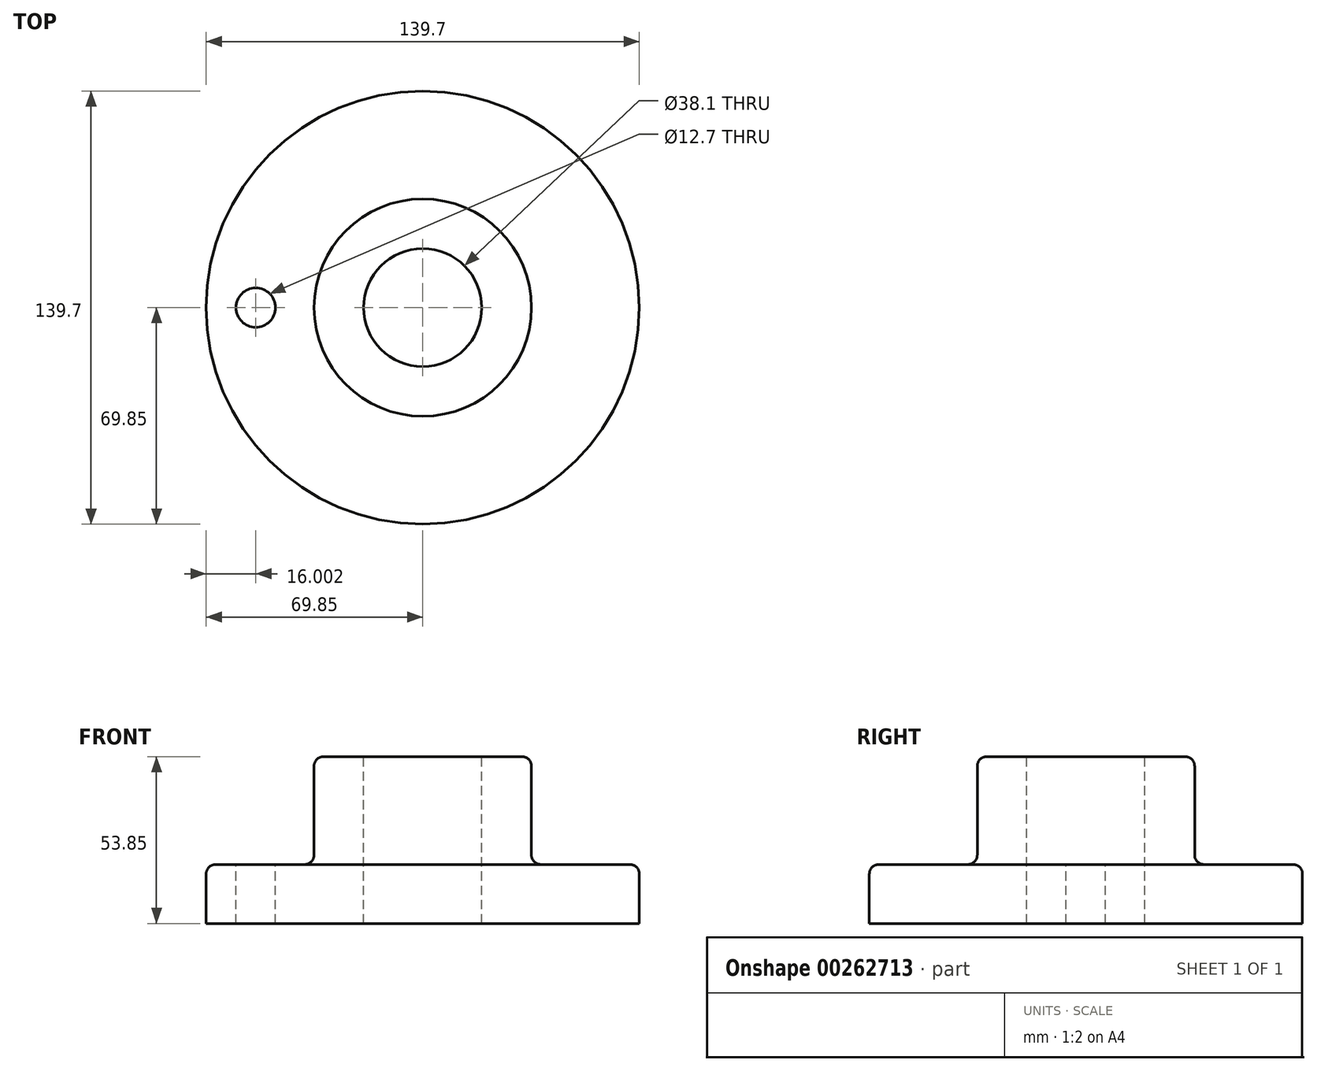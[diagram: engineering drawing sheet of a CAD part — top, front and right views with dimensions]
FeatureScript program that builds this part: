
annotation { "Feature Type Name" : "Feature", "Feature Type Description" : "" }
export const myFeature = defineFeature(function(context is Context, id is Id, definition is map)
    precondition{}
    {
        {
            var Q0;
            Q0=qCreatedBy(makeId("Front.planeOp"),FACE);
            var sketch = newSketch(context, id + "F0", { "sketchPlane" : qUnion([Q0])});
            skLineSegment(sketch, "E0", {"start": v(19.05, 34.8) * mm, "end": v(19.05, -19.05) * mm});
            skLineSegment(sketch, "E1", {"start": v(19.05, -19.05) * mm, "end": v(69.85, -19.05) * mm});
            skLineSegment(sketch, "E2", {"start": v(69.85, -19.05) * mm, "end": v(69.85, 0) * mm});
            skLineSegment(sketch, "E3", {"start": v(69.85, 0) * mm, "end": v(35.05, 0) * mm});
            skLineSegment(sketch, "E4", {"start": v(35.05, 0) * mm, "end": v(35.05, 34.8) * mm});
            skLineSegment(sketch, "E5", {"start": v(35.05, 34.8) * mm, "end": v(19.05, 34.8) * mm});
            skLineSegment(sketch, "E6", {"start": v(0, 35.4) * mm, "end": v(0, -19.17) * mm});
            skSolve(sketch);
        }
        {
            var Q0;
            Q0=makeQuery(id+"F0.imprint","IMPRINT",FACE,{"disambiguationData":[TD([[makeQuery(id+"F0.imprint","IMPRINT",EDGE,{"derivedFrom":sQuery(id+"F0.wireOp",EDGE,"E0")}),1.0]])]});
            var Q1;
            Q1=sQuery(id+"F0.wireOp",EDGE,"E6");
            revolve(context, id + "F1", {"entities" : qUnion([Q0]), "axis" : qUnion([Q1]), "revolveType" : RevolveType.FULL});
        }
        {
            var Q0;
            Q0=makeQuery(id+"F1.opRevolve","SWEPT_FACE",FACE,{"disambiguationData":[OSD([sQuery(id+"F0.wireOp",EDGE,"E3")])]});
            var sketch = newSketch(context, id + "F2", { "sketchPlane" : qUnion([Q0])});
            skCircle(sketch, "E7", {"center": v(0, 0) * mm, "radius": 53.85 * mm});
            skCircle(sketch, "E8", {"center": v(-53.85, 0) * mm, "radius": 6.35 * mm});
            skSolve(sketch);
        }
        {
            var Q0;
            {var subQ0=sQuery(id+"F2.wireOp",EDGE,"E8");var subQ1=sQuery(id+"F2.wireOp",EDGE,"E7");var subQ2=makeQuery(id+"F2.imprint","INTERSECT",VERTEX,{"disambiguationData":[OD(0.0)],"derivedFrom":[subQ1,subQ0]});Q0=makeQuery(id+"F2.imprint","IMPRINT",FACE,{"disambiguationData":[TD([[makeQuery(id+"F2.imprint","IMPRINT",EDGE,{"disambiguationData":[TD([[subQ2,1.0]])],"derivedFrom":subQ1}),-1.0]])]});}
            var Q1;
            {var subQ0=sQuery(id+"F2.wireOp",EDGE,"E8");var subQ1=sQuery(id+"F2.wireOp",EDGE,"E7");var subQ2=makeQuery(id+"F2.imprint","INTERSECT",VERTEX,{"disambiguationData":[OD(0.0)],"derivedFrom":[subQ1,subQ0]});Q1=makeQuery(id+"F2.imprint","IMPRINT",FACE,{"disambiguationData":[TD([[makeQuery(id+"F2.imprint","IMPRINT",EDGE,{"disambiguationData":[TD([[subQ2,1.0]])],"derivedFrom":subQ1}),1.0]])]});}
            var Q2;
            {var subQ0=sQuery(id+"FVgml1rrUZP4tpZ_1.3.F2.wireOp",EDGE,"E8");var subQ1=sQuery(id+"FVgml1rrUZP4tpZ_1.3.F2.wireOp",EDGE,"E7");var subQ2=makeQuery(id+"FVgml1rrUZP4tpZ_1.3.F2.imprint","INTERSECT",VERTEX,{"disambiguationData":[OD(0.0)],"derivedFrom":[subQ1,subQ0]});Q2=makeQuery(id+"FVgml1rrUZP4tpZ_1.3.F2.imprint","IMPRINT",FACE,{"disambiguationData":[TD([[makeQuery(id+"FVgml1rrUZP4tpZ_1.3.F2.imprint","IMPRINT",EDGE,{"disambiguationData":[TD([[subQ2,1.0]])],"derivedFrom":subQ1}),1.0]])]});}
            var Q3;
            {var subQ0=sQuery(id+"FVgml1rrUZP4tpZ_1.3.F2.wireOp",EDGE,"E8");var subQ1=sQuery(id+"FVgml1rrUZP4tpZ_1.3.F2.wireOp",EDGE,"E7");var subQ2=makeQuery(id+"FVgml1rrUZP4tpZ_1.3.F2.imprint","INTERSECT",VERTEX,{"disambiguationData":[OD(0.0)],"derivedFrom":[subQ1,subQ0]});Q3=makeQuery(id+"FVgml1rrUZP4tpZ_1.3.F2.imprint","IMPRINT",FACE,{"disambiguationData":[TD([[makeQuery(id+"FVgml1rrUZP4tpZ_1.3.F2.imprint","IMPRINT",EDGE,{"disambiguationData":[TD([[subQ2,1.0]])],"derivedFrom":subQ1}),-1.0]])]});}
            var Q4;
            {var subQ0=sQuery(id+"FVgml1rrUZP4tpZ_1.2.F2.wireOp",EDGE,"E8");var subQ1=sQuery(id+"FVgml1rrUZP4tpZ_1.2.F2.wireOp",EDGE,"E7");var subQ2=makeQuery(id+"FVgml1rrUZP4tpZ_1.2.F2.imprint","INTERSECT",VERTEX,{"disambiguationData":[OD(0.0)],"derivedFrom":[subQ1,subQ0]});Q4=makeQuery(id+"FVgml1rrUZP4tpZ_1.2.F2.imprint","IMPRINT",FACE,{"disambiguationData":[TD([[makeQuery(id+"FVgml1rrUZP4tpZ_1.2.F2.imprint","IMPRINT",EDGE,{"disambiguationData":[TD([[subQ2,1.0]])],"derivedFrom":subQ1}),1.0]])]});}
            var Q5;
            {var subQ0=sQuery(id+"FVgml1rrUZP4tpZ_1.2.F2.wireOp",EDGE,"E8");var subQ1=sQuery(id+"FVgml1rrUZP4tpZ_1.2.F2.wireOp",EDGE,"E7");var subQ2=makeQuery(id+"FVgml1rrUZP4tpZ_1.2.F2.imprint","INTERSECT",VERTEX,{"disambiguationData":[OD(0.0)],"derivedFrom":[subQ1,subQ0]});Q5=makeQuery(id+"FVgml1rrUZP4tpZ_1.2.F2.imprint","IMPRINT",FACE,{"disambiguationData":[TD([[makeQuery(id+"FVgml1rrUZP4tpZ_1.2.F2.imprint","IMPRINT",EDGE,{"disambiguationData":[TD([[subQ2,1.0]])],"derivedFrom":subQ1}),-1.0]])]});}
            var Q6;
            {var subQ0=sQuery(id+"FVgml1rrUZP4tpZ_1.1.F2.wireOp",EDGE,"E8");var subQ1=sQuery(id+"FVgml1rrUZP4tpZ_1.1.F2.wireOp",EDGE,"E7");var subQ2=makeQuery(id+"FVgml1rrUZP4tpZ_1.1.F2.imprint","INTERSECT",VERTEX,{"disambiguationData":[OD(0.0)],"derivedFrom":[subQ1,subQ0]});Q6=makeQuery(id+"FVgml1rrUZP4tpZ_1.1.F2.imprint","IMPRINT",FACE,{"disambiguationData":[TD([[makeQuery(id+"FVgml1rrUZP4tpZ_1.1.F2.imprint","IMPRINT",EDGE,{"disambiguationData":[TD([[subQ2,1.0]])],"derivedFrom":subQ1}),-1.0]])]});}
            var Q7;
            {var subQ0=sQuery(id+"FVgml1rrUZP4tpZ_1.1.F2.wireOp",EDGE,"E8");var subQ1=sQuery(id+"FVgml1rrUZP4tpZ_1.1.F2.wireOp",EDGE,"E7");var subQ2=makeQuery(id+"FVgml1rrUZP4tpZ_1.1.F2.imprint","INTERSECT",VERTEX,{"disambiguationData":[OD(0.0)],"derivedFrom":[subQ1,subQ0]});Q7=makeQuery(id+"FVgml1rrUZP4tpZ_1.1.F2.imprint","IMPRINT",FACE,{"disambiguationData":[TD([[makeQuery(id+"FVgml1rrUZP4tpZ_1.1.F2.imprint","IMPRINT",EDGE,{"disambiguationData":[TD([[subQ2,1.0]])],"derivedFrom":subQ1}),1.0]])]});}
            extrude(context, id + "F3", {"entities" : qUnion([Q0, Q1, Q2, Q3, Q4, Q5, Q6, Q7]), "operationType" : NewBodyOperationType.REMOVE, "oppositeDirection" : true, "depth" : 25.4 * mm});
        }
        {
            var Q0;
            Q0=makeQuery(id+"F1.opRevolve","SWEPT_EDGE",EDGE,{"disambiguationData":[OSD([sQuery(id+"F0.wireOp",EDGE,"E4"),sQuery(id+"F0.wireOp",EDGE,"E5")])]});
            var Q1;
            Q1=makeQuery(id+"F1.opRevolve","SWEPT_EDGE",EDGE,{"disambiguationData":[OSD([sQuery(id+"F0.wireOp",EDGE,"E3"),sQuery(id+"F0.wireOp",EDGE,"E4")])]});
            var Q2;
            Q2=makeQuery(id+"F1.opRevolve","SWEPT_EDGE",EDGE,{"disambiguationData":[OSD([sQuery(id+"F0.wireOp",EDGE,"E2"),sQuery(id+"F0.wireOp",EDGE,"E3")])]});
            fillet(context, id + "F4", {"entities" : qUnion([Q0, Q1, Q2]), "radius" : 3.05 * mm, "tangentPropagation" : true, "allowEdgeOverflow" : false});
        }
    });
